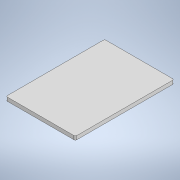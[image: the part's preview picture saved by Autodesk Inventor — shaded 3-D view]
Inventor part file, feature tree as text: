
AUTODESK INVENTOR PART (.ipt)
format: ipt  version: 2021 (Build 250183000, 183)  size: 115,200 bytes
history: native  units: mm
features: extrude x2, sketch x2, other x1, fillet x1
ambient origin geometry x8: Origin, YZ Plane, XZ Plane, XY Plane, X Axis, Y Axis, Z Axis, Center Point
bodies: Body1 (feature_tree)
feature tree (6):
  other  "Bryła1"
  extrude  "Wyciągnięcie proste1"  Depth=190.0mm
  fillet  "Zaokrąglenie1"  Radius=270.0mm
  extrude  "Wyciągnięcie proste3"  Depth=10.0mm TaperAngle=0.0deg
  sketch  "Szkic2"
  sketch  "Szkic4"
